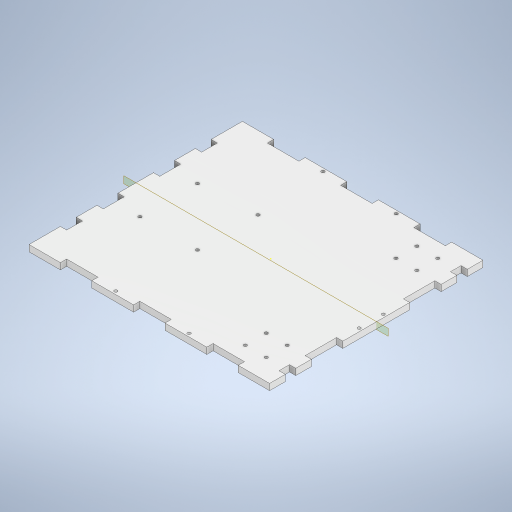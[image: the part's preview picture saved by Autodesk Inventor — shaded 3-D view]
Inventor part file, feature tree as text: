
AUTODESK INVENTOR PART (.ipt)
format: ipt  version: 2024.2 (Build 282272000, 272)  size: 418,816 bytes
history: native  units: mm
features: other x7, sketch x6, reference x6, extrude x5, mirror x1
ambient origin geometry x8: Origin, YZ Plane, XZ Plane, XY Plane, X Axis, Y Axis, Z Axis, Center Point
bodies: Body1 (feature_tree)
feature tree (25):
  other  "Твердое тело1"
  extrude  "Выдавливание1"  Depth=230.0mm
  sketch  "Эскиз2"
  extrude  "Выдавливание3"  Depth=204.0mm
  extrude  "Выдавливание4"  Depth=6.0mm
  other  "РабПлоскость1"
  mirror  "Зеркальное отражение1"
  extrude  "Выдавливание5"  Depth=30.0mm
  extrude  "Выдавливание6"  Depth=30.0mm
  sketch  "Эскиз1"
  sketch  "Эскиз5"
  sketch  "Эскиз6"
  reference  "Ссылка1"
  reference  "Ссылка2"
  sketch  "Эскиз7"
  reference  "Ссылка3"
  reference  "Ссылка4"
  reference  "Ссылка5"
  reference  "Ссылка6"
  sketch  "Эскиз9"
  other  "<userpath>\Documents\Artist-v2\3D\Робот.iam"
  other  "Робот.iam"
  other  "бок:2"
  other  "бок:1"
  other  "перед:1"
